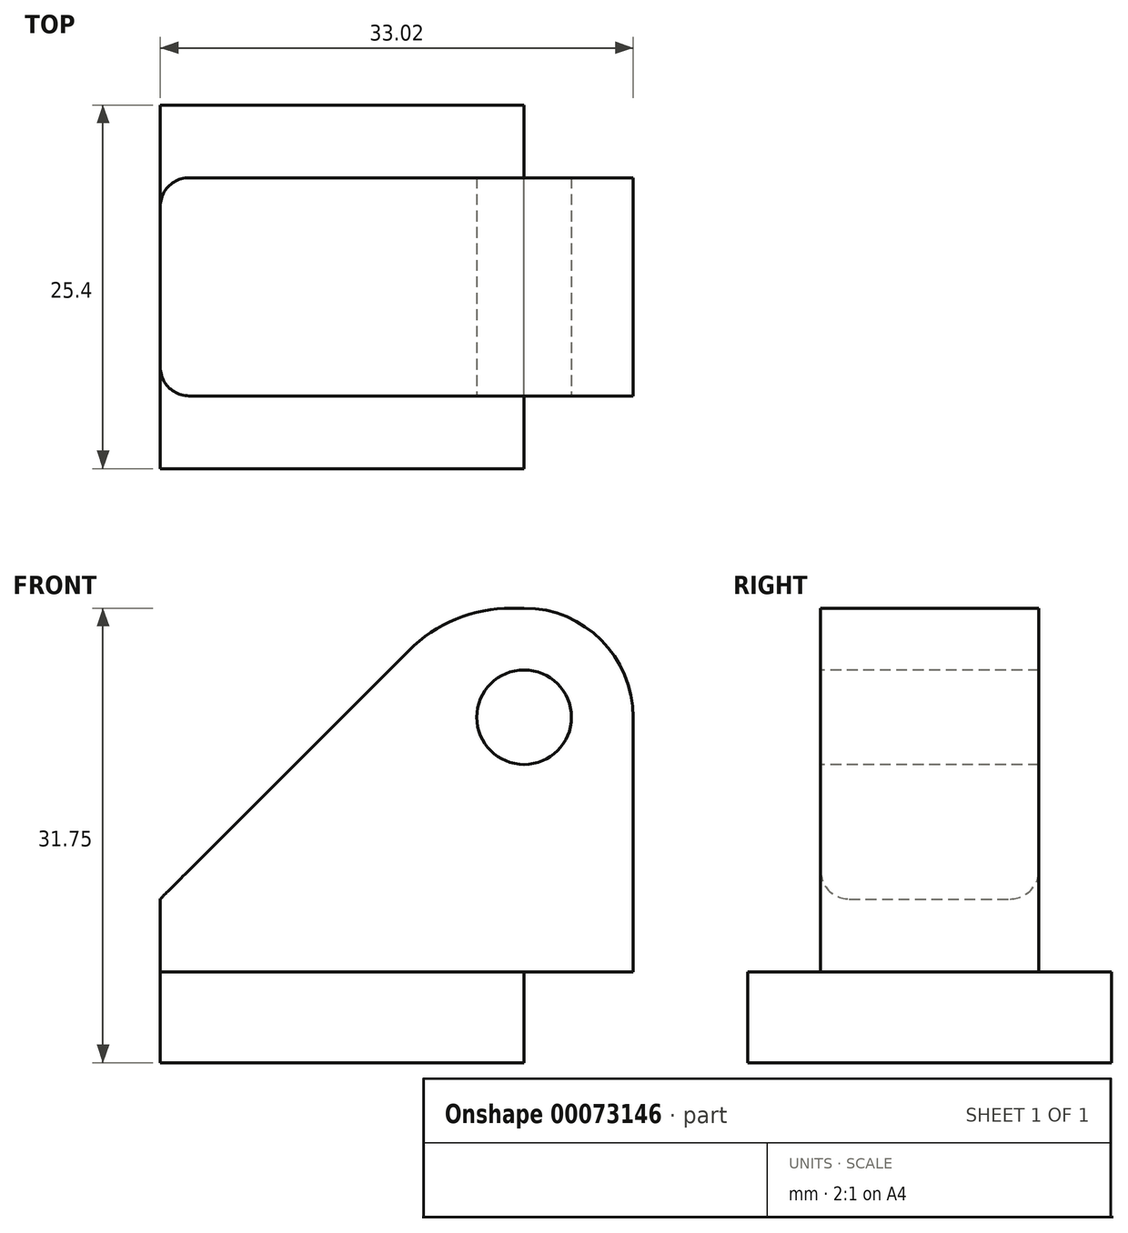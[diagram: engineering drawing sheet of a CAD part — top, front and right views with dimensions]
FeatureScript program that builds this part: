
annotation { "Feature Type Name" : "Feature", "Feature Type Description" : "" }
export const myFeature = defineFeature(function(context is Context, id is Id, definition is map)
    precondition{}
    {
        {
            var Q0;
            Q0=qCreatedBy(makeId("Top.planeOp"),FACE);
            var sketch = newSketch(context, id + "F0", { "sketchPlane" : qUnion([Q0])});
            skLineSegment(sketch, "E0.rect.bottom", {"start": v(12.7, -12.7) * mm, "end": v(-12.7, -12.7) * mm});
            skLineSegment(sketch, "E0.rect.top", {"start": v(12.7, 12.7) * mm, "end": v(-12.7, 12.7) * mm});
            skLineSegment(sketch, "E0.rect.left", {"start": v(12.7, -12.7) * mm, "end": v(12.7, 12.7) * mm});
            skLineSegment(sketch, "E0.rect.right", {"start": v(-12.7, -12.7) * mm, "end": v(-12.7, 12.7) * mm});
            skPoint(sketch, "E0.rect.middle", {"position": v(0, 0) * mm});
            skSolve(sketch);
        }
        {
            var Q0;
            Q0 = qSketchRegion(id + "F0", true);
            extrude(context, id + "F1", {"entities" : qUnion([Q0]), "depth" : 6.35 * mm});
        }
        {
            var Q0;
            Q0=makeQuery(id+"F1.opExtrude","CAP_FACE",FACE,{"disambiguationData":[OSD([sQuery(id+"F0.wireOp",EDGE,"E0.rect.bottom"),sQuery(id+"F0.wireOp",EDGE,"E0.rect.top"),sQuery(id+"F0.wireOp",EDGE,"E0.rect.left"),sQuery(id+"F0.wireOp",EDGE,"E0.rect.right")])],"isStart":false});
            var sketch = newSketch(context, id + "F2", { "sketchPlane" : qUnion([Q0])});
            skLineSegment(sketch, "E1.rect.bottom", {"start": v(12.7, -7.62) * mm, "end": v(-12.7, -7.62) * mm});
            skLineSegment(sketch, "E1.rect.top", {"start": v(12.7, 7.62) * mm, "end": v(-12.7, 7.62) * mm});
            skLineSegment(sketch, "E1.rect.left", {"start": v(12.7, -7.62) * mm, "end": v(12.7, 7.62) * mm});
            skLineSegment(sketch, "E1.rect.right", {"start": v(-12.7, -7.62) * mm, "end": v(-12.7, 7.62) * mm});
            skPoint(sketch, "E1.rect.middle", {"position": v(0, 0) * mm});
            skLineSegment(sketch, "E2.bottom", {"start": v(12.7, 7.62) * mm, "end": v(20.32, 7.62) * mm});
            skLineSegment(sketch, "E2.top", {"start": v(12.7, -7.62) * mm, "end": v(20.32, -7.62) * mm});
            skLineSegment(sketch, "E2.left", {"start": v(12.7, 7.62) * mm, "end": v(12.7, -7.62) * mm});
            skLineSegment(sketch, "E2.right", {"start": v(20.32, 7.62) * mm, "end": v(20.32, -7.62) * mm});
            skLineSegment(sketch, "E3.bottom", {"start": v(-12.7, -7.62) * mm, "end": v(-20.32, -7.62) * mm});
            skLineSegment(sketch, "E3.top", {"start": v(-12.7, 7.72) * mm, "end": v(-20.32, 7.72) * mm});
            skLineSegment(sketch, "E3.left", {"start": v(-12.7, -7.62) * mm, "end": v(-12.7, 7.72) * mm});
            skLineSegment(sketch, "E3.right", {"start": v(-20.32, -7.62) * mm, "end": v(-20.32, 7.72) * mm});
            skSolve(sketch);
        }
        {
            var Q0;
            {var subQ0=sQuery(id+"F2.wireOp",EDGE,"E1.rect.bottom");Q0=makeQuery(id+"F2.imprint","IMPRINT",FACE,{"disambiguationData":[TD([[makeQuery(id+"F2.imprint","IMPRINT",EDGE,{"derivedFrom":subQ0}),-1.0]])]});}
            var Q1;
            Q1=makeQuery(id+"F2.imprint","IMPRINT",FACE,{"disambiguationData":[TD([[makeQuery(id+"F2.imprint","IMPRINT",EDGE,{"derivedFrom":sQuery(id+"F2.wireOp",EDGE,"E2.bottom")}),-1.0]])]});
            extrude(context, id + "F3", {"entities" : qUnion([Q0, Q1]), "operationType" : NewBodyOperationType.ADD, "depth" : 25.4 * mm});
        }
        {
            var Q0;
            Q0=makeQuery(id+"F3.opExtrude","CAP_EDGE",EDGE,{"disambiguationData":[OSD([sQuery(id+"F2.wireOp",EDGE,"E1.rect.left")])],"isStart":false});
            var Q1;
            Q1=makeQuery(id+"F3.opExtrude","CAP_EDGE",EDGE,{"disambiguationData":[OSD([sQuery(id+"F2.wireOp",EDGE,"E2.right")])],"isStart":false});
            fillet(context, id + "F4", {"entities" : qUnion([Q0, Q1]), "radius" : 7.62 * mm, "tangentPropagation" : true, "allowEdgeOverflow" : false});
        }
        {
            var Q0;
            Q0=makeQuery(id+"F3.opExtrude","CAP_EDGE",EDGE,{"disambiguationData":[OSD([sQuery(id+"F2.wireOp",EDGE,"E1.rect.right")])],"isStart":false});
            var Q1;
            Q1=makeQuery(id+"F3.opExtrude","CAP_EDGE",EDGE,{"disambiguationData":[OSD([sQuery(id+"F2.wireOp",EDGE,"E3.left")])],"isStart":false});
            chamfer(context, id + "F5", {"entities" : qUnion([Q0, Q1]), "width" : 20.32 * mm, "tangentPropagation" : true});
        }
        {
            var Q0;
            {var subQ0=sQuery(id+"F2.wireOp",EDGE,"E1.rect.right");Q0=makeQuery(id+"F5.opChamfer","BLEND_EDGE",EDGE,{"blendedFrom":[makeQuery(id+"F3.opExtrude","CAP_EDGE",EDGE,{"disambiguationData":[OSD([subQ0])],"isStart":false}),makeQuery(id+"F3.opExtrude","CAP_FACE",FACE,{"disambiguationData":[OSD([sQuery(id+"F2.wireOp",EDGE,"E1.rect.bottom"),sQuery(id+"F2.wireOp",EDGE,"E1.rect.top"),sQuery(id+"F2.wireOp",EDGE,"E1.rect.left"),subQ0])],"isStart":false})],"blendedInto":[makeQuery(id+"F3.opExtrude","CAP_FACE",FACE,{"disambiguationData":[OSD([sQuery(id+"F2.wireOp",EDGE,"E1.rect.bottom"),sQuery(id+"F2.wireOp",EDGE,"E1.rect.top"),sQuery(id+"F2.wireOp",EDGE,"E1.rect.left"),subQ0])],"isStart":false})]});}
            var Q1;
            {var subQ0=sQuery(id+"F2.wireOp",EDGE,"E3.left");Q1=makeQuery(id+"F5.opChamfer","BLEND_EDGE",EDGE,{"blendedFrom":[makeQuery(id+"F3.opExtrude","CAP_EDGE",EDGE,{"disambiguationData":[OSD([subQ0])],"isStart":false}),makeQuery(id+"F3.opExtrude","CAP_FACE",FACE,{"disambiguationData":[OSD([sQuery(id+"F2.wireOp",EDGE,"E1.rect.bottom"),sQuery(id+"F2.wireOp",EDGE,"E1.rect.top"),sQuery(id+"F2.wireOp",EDGE,"E2.bottom"),sQuery(id+"F2.wireOp",EDGE,"E2.top"),sQuery(id+"F2.wireOp",EDGE,"E2.right"),subQ0])],"isStart":false})],"blendedInto":[makeQuery(id+"F3.opExtrude","CAP_FACE",FACE,{"disambiguationData":[OSD([sQuery(id+"F2.wireOp",EDGE,"E1.rect.bottom"),sQuery(id+"F2.wireOp",EDGE,"E1.rect.top"),sQuery(id+"F2.wireOp",EDGE,"E2.bottom"),sQuery(id+"F2.wireOp",EDGE,"E2.top"),sQuery(id+"F2.wireOp",EDGE,"E2.right"),subQ0])],"isStart":false})]});}
            fillet(context, id + "F6", {"entities" : qUnion([Q0, Q1]), "radius" : 10.16 * mm, "tangentPropagation" : true, "allowEdgeOverflow" : false});
        }
        {
            var Q0;
            Q0=makeQuery(id+"F3.opExtrude","SWEPT_FACE",FACE,{"disambiguationData":[OSD([sQuery(id+"F2.wireOp",EDGE,"E1.rect.bottom"),sQuery(id+"F2.wireOp",EDGE,"E2.top")])]});
            var sketch = newSketch(context, id + "F7", { "sketchPlane" : qUnion([Q0])});
            skCircle(sketch, "E4", {"center": v(12.7, 24.13) * mm, "radius": 3.3 * mm});
            skSolve(sketch);
        }
        {
            var Q0;
            Q0=makeQuery(id+"F7.imprint","IMPRINT",FACE,{"disambiguationData":[TD([[makeQuery(id+"F7.imprint","IMPRINT",EDGE,{"derivedFrom":sQuery(id+"F7.wireOp",EDGE,"E4")}),1.0]])]});
            extrude(context, id + "F8", {"entities" : qUnion([Q0]), "operationType" : NewBodyOperationType.REMOVE, "endBound" : BoundingType.THROUGH_ALL, "oppositeDirection" : true, "depth" : 25.4 * mm});
        }
        {
            var Q0;
            Q0=makeQuery(id+"F5.opChamfer","BLEND_EDGE",EDGE,{"blendedFrom":[makeQuery(id+"F3.opExtrude","CAP_EDGE",EDGE,{"disambiguationData":[OSD([sQuery(id+"F2.wireOp",EDGE,"E3.left")])],"isStart":false}),makeQuery(id+"F3.opExtrude","SWEPT_FACE",FACE,{"disambiguationData":[OSD([sQuery(id+"F2.wireOp",EDGE,"E1.rect.bottom"),sQuery(id+"F2.wireOp",EDGE,"E2.top")])]})],"blendedInto":[makeQuery(id+"F3.opExtrude","SWEPT_FACE",FACE,{"disambiguationData":[OSD([sQuery(id+"F2.wireOp",EDGE,"E1.rect.bottom"),sQuery(id+"F2.wireOp",EDGE,"E2.top")])]})]});
            var Q1;
            Q1=makeQuery(id+"F5.opChamfer","BLEND_EDGE",EDGE,{"blendedFrom":[makeQuery(id+"F3.opExtrude","CAP_EDGE",EDGE,{"disambiguationData":[OSD([sQuery(id+"F2.wireOp",EDGE,"E3.left")])],"isStart":false}),makeQuery(id+"F3.opExtrude","SWEPT_FACE",FACE,{"disambiguationData":[OSD([sQuery(id+"F2.wireOp",EDGE,"E1.rect.top"),sQuery(id+"F2.wireOp",EDGE,"E2.bottom")])]})],"blendedInto":[makeQuery(id+"F3.opExtrude","SWEPT_FACE",FACE,{"disambiguationData":[OSD([sQuery(id+"F2.wireOp",EDGE,"E1.rect.top"),sQuery(id+"F2.wireOp",EDGE,"E2.bottom")])]})]});
            var Q2;
            {var subQ0=sQuery(id+"F2.wireOp",EDGE,"E3.left");Q2=makeQuery(id+"F5.opChamfer","BLEND_EDGE",EDGE,{"blendedFrom":[makeQuery(id+"F3.opExtrude","CAP_EDGE",EDGE,{"disambiguationData":[OSD([subQ0])],"isStart":false}),makeQuery(id+"F3.boolean.opBoolean","MERGE",FACE,{"derivedFrom":[makeQuery(id+"F1.opExtrude","SWEPT_FACE",FACE,{"disambiguationData":[OSD([sQuery(id+"F0.wireOp",EDGE,"E0.rect.right")])]}),makeQuery(id+"F3.opExtrude","SWEPT_FACE",FACE,{"disambiguationData":[OSD([subQ0])]})]})],"blendedInto":[makeQuery(id+"F3.boolean.opBoolean","MERGE",FACE,{"derivedFrom":[makeQuery(id+"F1.opExtrude","SWEPT_FACE",FACE,{"disambiguationData":[OSD([sQuery(id+"F0.wireOp",EDGE,"E0.rect.right")])]}),makeQuery(id+"F3.opExtrude","SWEPT_FACE",FACE,{"disambiguationData":[OSD([subQ0])]})]})]});}
            var Q3;
            Q3=makeQuery(id+"F3.opExtrude","SWEPT_EDGE",EDGE,{"disambiguationData":[OSD([sQuery(id+"F0.wireOp",EDGE,"E0.rect.right"),sQuery(id+"F2.wireOp",EDGE,"E1.rect.bottom"),sQuery(id+"F2.wireOp",EDGE,"E3.bottom"),sQuery(id+"F2.wireOp",EDGE,"E3.left")])]});
            var Q4;
            Q4=makeQuery(id+"F3.opExtrude","SWEPT_EDGE",EDGE,{"disambiguationData":[OSD([sQuery(id+"F2.wireOp",EDGE,"E1.rect.top"),sQuery(id+"F2.wireOp",EDGE,"E3.left")])]});
            fillet(context, id + "F9", {"entities" : qUnion([Q0, Q1, Q2, Q3, Q4]), "radius" : 2 * mm, "tangentPropagation" : true, "allowEdgeOverflow" : false});
        }
    });
